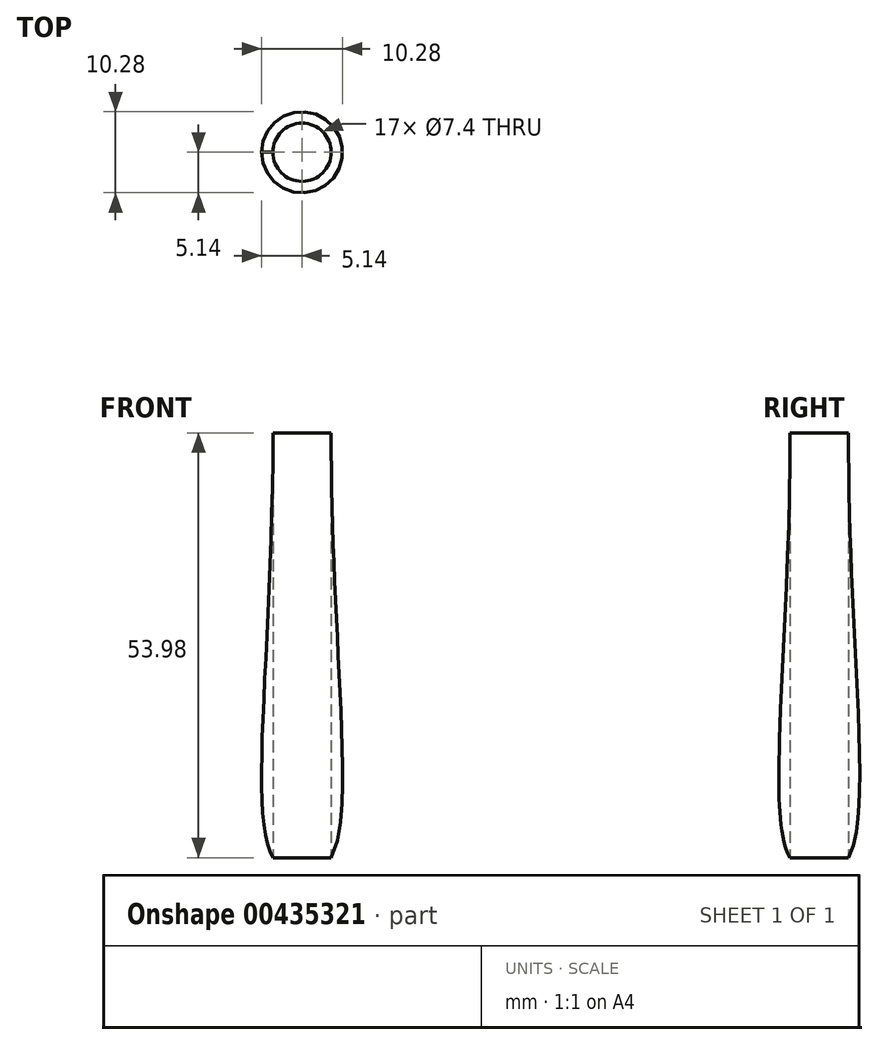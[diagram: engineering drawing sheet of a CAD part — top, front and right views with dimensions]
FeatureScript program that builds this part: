
annotation { "Feature Type Name" : "Feature", "Feature Type Description" : "" }
export const myFeature = defineFeature(function(context is Context, id is Id, definition is map)
    precondition{}
    {
        {
            var Q0;
            Q0=qCreatedBy(makeId("Front.planeOp"),FACE);
            var sketch = newSketch(context, id + "F0", { "sketchPlane" : qUnion([Q0])});
            skLineSegment(sketch, "E0.bottom", {"start": v(3.7, -26.99) * mm, "end": v(-3.7, -26.99) * mm});
            skLineSegment(sketch, "E0.top", {"start": v(3.7, 26.99) * mm, "end": v(-3.7, 26.99) * mm});
            skLineSegment(sketch, "E0.left", {"start": v(3.7, -26.99) * mm, "end": v(3.7, 26.99) * mm});
            skLineSegment(sketch, "E0.right", {"start": v(-3.7, -26.99) * mm, "end": v(-3.7, 26.99) * mm});
            skPoint(sketch, "E0.middle", {"position": v(0, 0) * mm});
            skLineSegment(sketch, "E1", {"start": v(0, -26.99) * mm, "end": v(0, 26.99) * mm});
            skFitSpline(sketch, "E2", {"points": [v(-3.7, 26.99) * mm, v(-3.7, -26.99) * mm, v(12.44, -6.69) * mm], "startDerivative": vector(0, -137.08) * mm, "endDerivative": vector(62.42, 145.14) * mm});
            skSolve(sketch);
        }
        {
            var Q0;
            {var subQ0=sQuery(id+"F0.wireOp",EDGE,"E0.right");Q0=makeQuery(id+"F0.imprint","IMPRINT",FACE,{"disambiguationData":[TD([[makeQuery(id+"F0.imprint","IMPRINT",EDGE,{"derivedFrom":subQ0}),1.0]])]});}
            var Q1;
            Q1=sQuery(id+"F0.wireOp",EDGE,"E1");
            revolve(context, id + "F1", {"entities" : qUnion([Q0]), "axis" : qUnion([Q1]), "revolveType" : RevolveType.FULL});
        }
    });
